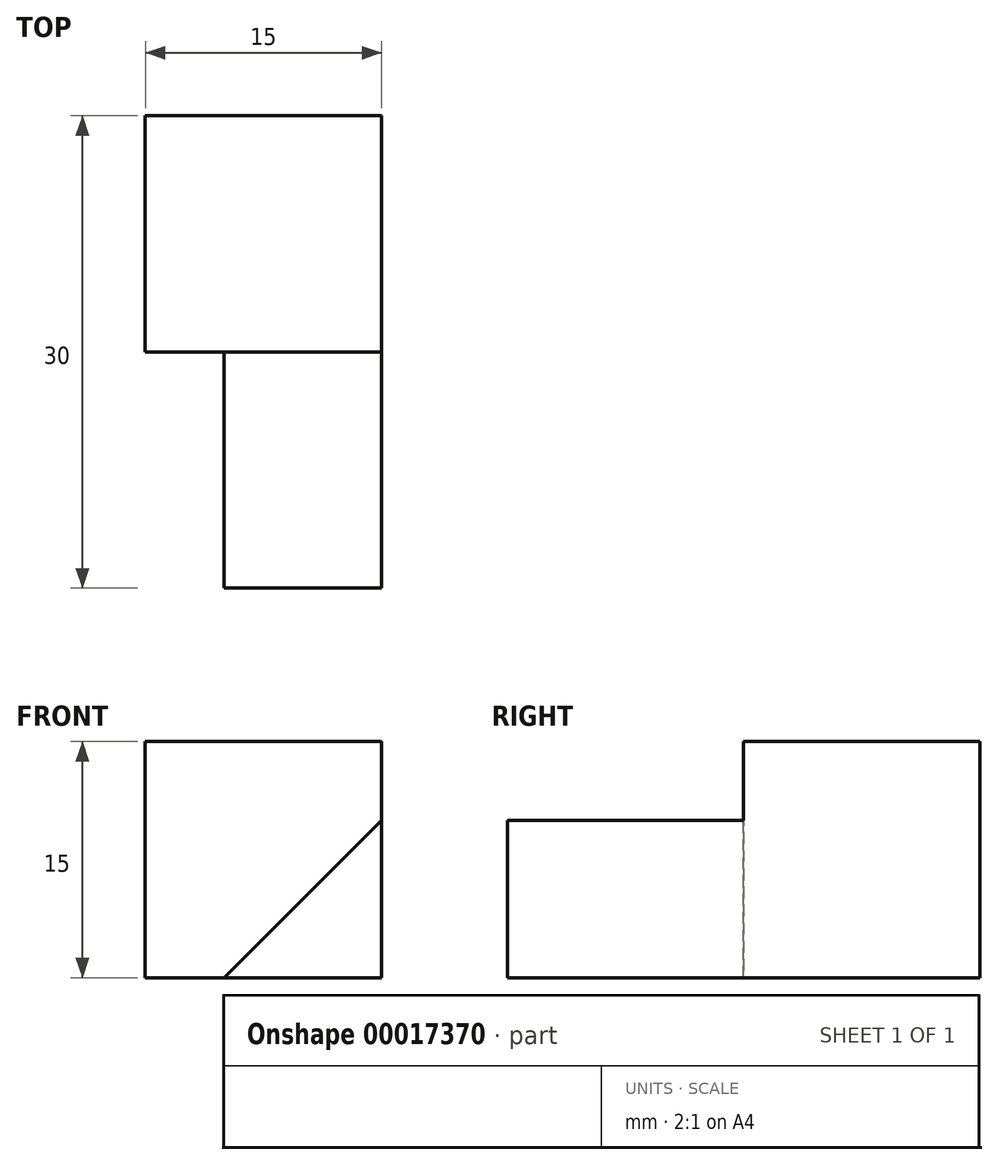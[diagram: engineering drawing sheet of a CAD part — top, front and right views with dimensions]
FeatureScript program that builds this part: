
annotation { "Feature Type Name" : "Feature", "Feature Type Description" : "" }
export const myFeature = defineFeature(function(context is Context, id is Id, definition is map)
    precondition{}
    {
        {
            var Q0;
            Q0=qCreatedBy(makeId("Front.planeOp"),FACE);
            var sketch = newSketch(context, id + "F0", { "sketchPlane" : qUnion([Q0])});
            skLineSegment(sketch, "E0.bottom", {"start": v(-10.03, 7.85) * mm, "end": v(4.97, 7.85) * mm});
            skLineSegment(sketch, "E0.top", {"start": v(-10.03, -7.15) * mm, "end": v(4.97, -7.15) * mm});
            skLineSegment(sketch, "E0.left", {"start": v(-10.03, 7.85) * mm, "end": v(-10.03, -7.15) * mm});
            skLineSegment(sketch, "E0.right", {"start": v(4.97, 7.85) * mm, "end": v(4.97, -7.15) * mm});
            skSolve(sketch);
        }
        {
            var Q0;
            Q0=makeQuery(id+"F0.imprint","IMPRINT",FACE,{"disambiguationData":[TD([[makeQuery(id+"F0.imprint","IMPRINT",EDGE,{"derivedFrom":sQuery(id+"F0.wireOp",EDGE,"E0.bottom")}),-1.0]])]});
            extrude(context, id + "F1", {"entities" : qUnion([Q0]), "depth" : 15 * mm});
        }
        {
            var Q0;
            Q0=makeQuery(id+"F1.opExtrude","CAP_FACE",FACE,{"disambiguationData":[OSD([sQuery(id+"F0.wireOp",EDGE,"E0.bottom"),sQuery(id+"F0.wireOp",EDGE,"E0.top"),sQuery(id+"F0.wireOp",EDGE,"E0.left"),sQuery(id+"F0.wireOp",EDGE,"E0.right")])],"isStart":false});
            var sketch = newSketch(context, id + "F2", { "sketchPlane" : qUnion([Q0])});
            skLineSegment(sketch, "E1", {"start": v(4.97, 2.85) * mm, "end": v(4.97, -7.15) * mm});
            skLineSegment(sketch, "E2", {"start": v(4.97, -7.15) * mm, "end": v(-5.03, -7.15) * mm});
            skLineSegment(sketch, "E3", {"start": v(-5.03, -7.15) * mm, "end": v(4.97, 2.85) * mm});
            skSolve(sketch);
        }
        {
            var Q0;
            Q0=makeQuery(id+"F2.imprint","IMPRINT",FACE,{"disambiguationData":[TD([[makeQuery(id+"F2.imprint","IMPRINT",EDGE,{"derivedFrom":sQuery(id+"F2.wireOp",EDGE,"E1")}),-1.0]])]});
            extrude(context, id + "F3", {"entities" : qUnion([Q0]), "operationType" : NewBodyOperationType.ADD, "depth" : 15 * mm});
        }
    });
